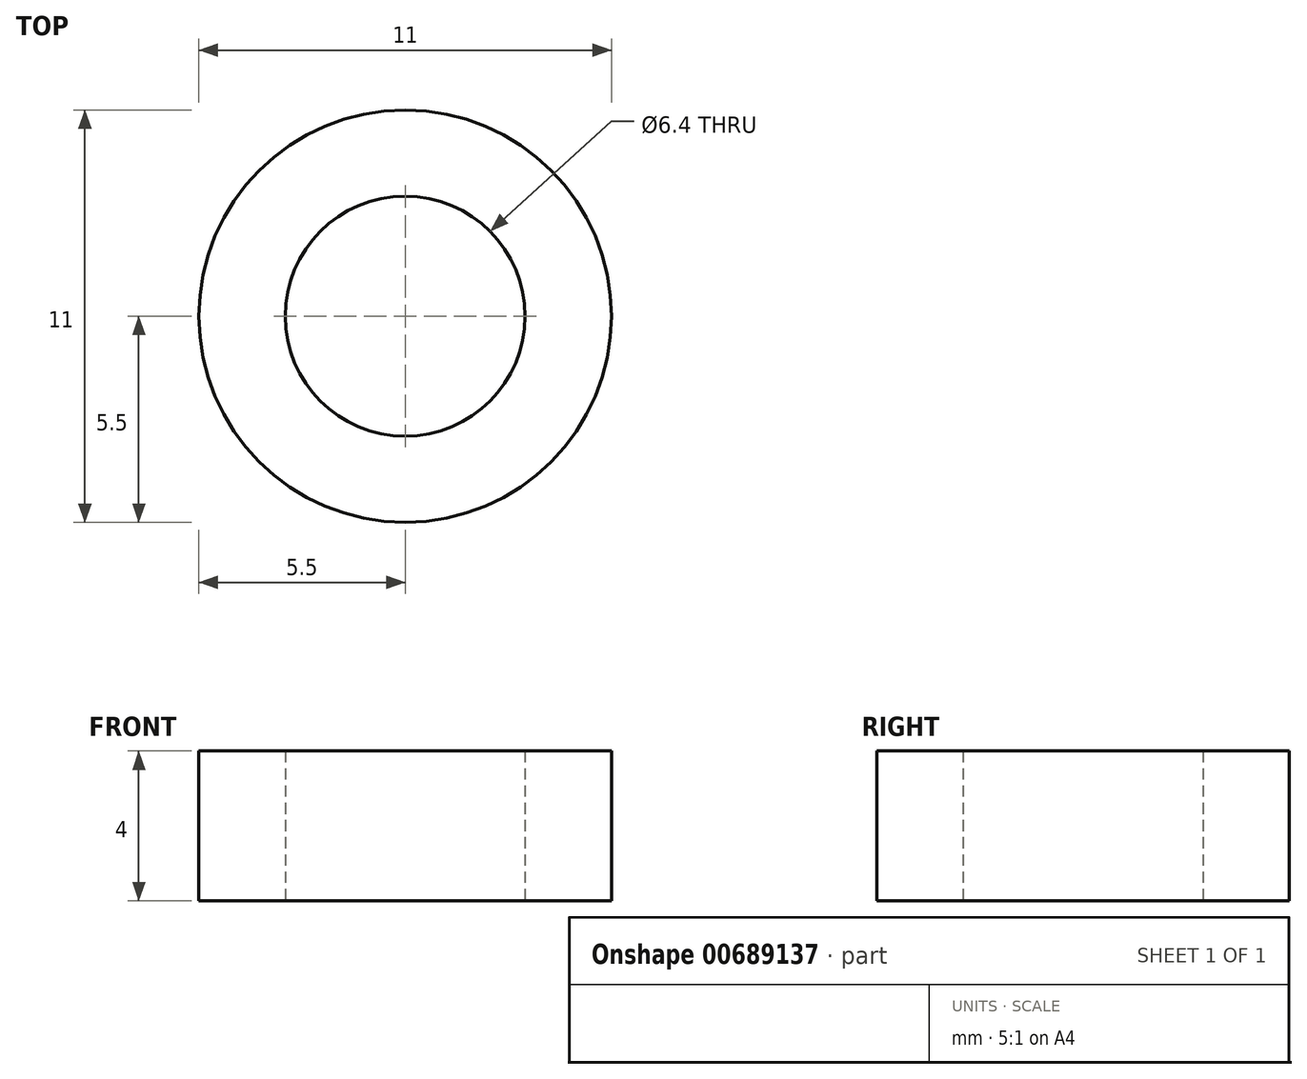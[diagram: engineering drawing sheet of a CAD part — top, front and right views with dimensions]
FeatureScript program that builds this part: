
annotation { "Feature Type Name" : "Feature", "Feature Type Description" : "" }
export const myFeature = defineFeature(function(context is Context, id is Id, definition is map)
    precondition{}
    {
        {
            var Q0;
            Q0=qCreatedBy(makeId("Top.planeOp"),FACE);
            var sketch = newSketch(context, id + "F0", { "sketchPlane" : qUnion([Q0])});
            skCircle(sketch, "E0", {"center": v(0, 0) * mm, "radius": 3.2 * mm});
            skCircle(sketch, "E1", {"center": v(0, 0) * mm, "radius": 5.5 * mm});
            skSolve(sketch);
        }
        {
            var Q0;
            Q0=makeQuery(id+"F0.imprint","IMPRINT",FACE,{"disambiguationData":[TD([[makeQuery(id+"F0.imprint","IMPRINT",EDGE,{"derivedFrom":sQuery(id+"F0.wireOp",EDGE,"E0")}),-1.0]])]});
            extrude(context, id + "F1", {"entities" : qUnion([Q0]), "depth" : 4 * mm, "offsetDistance" : 25 * mm});
        }
    });
